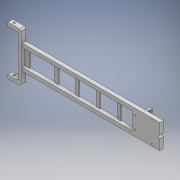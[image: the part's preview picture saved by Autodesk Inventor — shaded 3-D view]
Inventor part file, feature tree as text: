
AUTODESK INVENTOR PART (.ipt)
format: ipt  version: 2018 (Build 220112000, 112)  size: 599,552 bytes
history: native  units: mm
features: sketch x30, extrude x23, fillet x6, hole x5
ambient origin geometry x8: Origin, YZ Plane, XZ Plane, XY Plane, X Axis, Y Axis, Z Axis, Center Point
bodies: Solid1 (feature_tree)
feature tree (64):
  extrude  "Extrusion1"  Depth=50.0mm
  hole  "Hole1"  [1 undecoded]
  hole  "Hole2"  [1 undecoded]
  extrude  "Extrusion2"  Depth=25.0mm
  extrude  "Extrusion3"  Depth=25.0mm
  extrude  "Extrusion4"  Depth=5.0mm
  sketch  "Sketch7"  dims[d25=10.0mm d26=5.0mm]
  extrude  "Extrusion5"  Depth=5.0mm
  extrude  "Extrusion6"  Depth=35.0mm
  extrude  "Extrusion7"  Depth=35.0mm
  extrude  "Extrusion8"  Depth=35.0mm
  extrude  "Extrusion9"  Depth=2.0mm TaperAngle=0.0deg
  extrude  "Extrusion10"  Depth=7.5mm TaperAngle=0.0deg
  extrude  "Extrusion11"  Depth=10.0mm
  extrude  "Extrusion12"  Depth=7.5mm
  fillet  "Fillet1"  Radius=7.5mm
  fillet  "Fillet2"  Radius=25.0mm
  fillet  "Fillet3"  Radius=3.0mm
  fillet  "Fillet4"  Radius=3.2mm
  fillet  "Fillet5"  Radius=2.1mm
  fillet  "Fillet6"  Radius=5.5mm
  extrude  "Extrusion13"  Depth=92.5mm TaperAngle=0.0deg
  sketch  "Sketch17"  dims[d58=4.25mm d59=241.0mm d60=0.0mm]
  hole  "Hole3"  [1 undecoded]
  hole  "Hole4"  [1 undecoded]
  extrude  "Extrusion14"  Depth=5.0mm
  extrude  "Extrusion15"  Depth=2.5mm TaperAngle=0.0deg
  extrude  "Extrusion16"  Depth=30.0mm
  extrude  "Extrusion17"  Depth=2.5mm
  extrude  "Extrusion18"  Depth=14.55mm TaperAngle=0.0deg
  extrude  "Extrusion19"  Depth=0.1mm
  extrude  "Extrusion20"  Depth=3.25mm
  extrude  "Extrusion21"  Depth=3.25mm
  hole  "Hole5"  [1 undecoded]
  extrude  "Extrusion22"  Depth=2.0mm
  extrude  "Extrusion23"  Depth=7.5mm
  sketch  "Sketch1"  dims[d0=50.0mm d1=50.0mm]
  sketch  "Sketch2"  dims[d2=240.0mm d3=7.5mm]
  sketch  "Sketch3"  dims[d4=7.5mm d5=7.5mm d6=0.0mm]
  sketch  "Sketch4"  dims[d7=6.35mm d8=6.0mm d9=4.0mm d10=2.0mm d11=90.0deg d12=8.0mm d13=20.594885mm d14=25.0mm]
  sketch  "Sketch5"  dims[d15=3.3mm d16=6.0mm d17=4.0mm d18=2.0mm d19=90.0deg d20=8.0mm d21=20.594885mm d22=25.0mm]
  sketch  "Sketch6"  dims[d23=180.0deg d24=5.0mm]
  sketch  "Sketch8"  dims[d27=17.5mm d28=0.0mm d30=35.0mm]
  sketch  "Sketch9"  dims[d31=35.0mm d32=35.0mm]
  sketch  "Sketch10"  dims[d33=35.0mm d34=35.0mm]
  sketch  "Sketch11"  dims[d35=35.0mm d36=2.0mm d37=0.0mm]
  sketch  "Sketch12"  dims[d38=10.0mm d39=7.5mm d40=0.0mm]
  sketch  "Sketch13"  dims[d41=100.0mm d42=10.0mm]
  sketch  "Sketch14"  dims[d43=7.5mm d44=0.0mm d45=7.5mm d46=7.5mm d47=25.0mm d48=0.0mm d49=3.0mm d50=3.2mm d51=2.1mm d52=5.5mm]
  sketch  "Sketch15"  dims[d53=3.3mm d54=92.5mm d55=0.0mm]
  sketch  "Sketch16"  dims[d56=5.5mm d57=3.3mm]
  sketch  "Sketch18"  dims[d61=4.44mm d62=5.0mm]
  sketch  "Sketch19"  dims[d63=2.5mm d64=91.25mm d65=0.0mm]
  sketch  "Sketch20"  dims[d66=30.0mm d67=6.35mm]
  sketch  "Sketch21"  dims[d68=3.8mm d69=0.0mm d70=2.5mm]
  sketch  "Sketch22"  dims[d71=14.55mm d72=0.0mm d73=14.55mm d74=0.0mm]
  sketch  "Sketch23"  dims[d75=0.1mm d76=0.1mm]
  sketch  "Sketch24"  dims[d77=3.25mm d78=3.25mm]
  sketch  "Sketch25"  dims[d79=3.25mm d80=3.25mm]
  sketch  "Sketch26"  dims[d81=35.0mm d82=10.0mm]
  sketch  "Sketch27"  dims[d83=2.0mm d84=0.0mm d85=3.6mm]
  sketch  "Sketch28"  dims[d86=3.6mm]
  sketch  "Sketch29"  dims[d87=3.3mm d88=6.0mm d89=4.0mm d90=2.0mm d91=90.0deg d92=15.0mm d93=20.594885mm]
  sketch  "Sketch30"  dims[d94=3.3mm d95=6.0mm d96=4.0mm d97=2.0mm d98=90.0deg d99=15.0mm d100=20.594885mm d101=6.0mm d102=20.0mm d103=0.0mm d104=10.0mm d105=0.0mm d106=2.0mm d107=0.0mm d108=4.0mm d109=100.0mm d110=0.0mm d111=100.0mm d112=0.0mm d113=5.0mm d114=2.0mm d115=0.0mm d116=3.3mm d117=3.3mm d118=3.3mm d119=3.3mm d120=2.0mm d121=0.0mm d122=5.5mm d123=0.0mm d124=3.3mm d125=6.0mm d126=4.0mm d127=2.0mm d128=90.0deg d129=8.0mm d130=20.594885mm d131=42.0mm d132=17.0mm d133=21.0mm d135=8.5mm d136=15.825mm d137=3.5mm d138=21.0mm d139=3.3mm d140=3.3mm d141=3.3mm d142=10.0mm d143=0.0mm d144=7.5mm d145=0.0mm]
note: 5 required parameter values undecoded (feature->parameter linkage not recoverable at this tier; creation-order binding heuristic only, values carry confidence <= 0.55)
